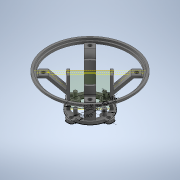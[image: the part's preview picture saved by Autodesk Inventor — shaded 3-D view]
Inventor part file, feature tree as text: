
AUTODESK INVENTOR PART (.ipt)
format: ipt  version: 2020 (Build 240168000, 168)  size: 606,208 bytes
history: native  units: mm
features: projected_geometry x28, sketch x16, extrude x9, other x5, pattern_circular x1, sweep x1
ambient origin geometry x8: Origin, YZ Plane, XZ Plane, XY Plane, X Axis, Y Axis, Z Axis, Center Point
bodies: Body1 (feature_tree)
feature tree (60):
  other  "Твердое тело1"
  sketch  "Эскиз1"
  extrude  "Выдавливание1"  Depth=44.0mm
  extrude  "Выдавливание2"  Depth=4.0mm
  sketch  "Эскиз3"
  extrude  "Выдавливание4"  Depth=40.0mm TaperAngle=360.0deg
  pattern_circular  "Круговой массив1"  [2 undecoded]
  other  "РабПлоскость2"
  sketch  "Эскиз5"
  other  "РабПлоскость1"
  sketch  "Эскиз6"
  sketch  "Эскиз7"
  extrude  "Выдавливание6"  Depth=4.5mm
  sketch  "Эскиз8"
  extrude  "Выдавливание7"  Depth=3.0mm
  sketch  "Эскиз9"
  other  "РабПлоскость3"
  sketch  "Эскиз10"
  sweep  "Сдвиг1"
  extrude  "Выдавливание8"  Depth=1.0mm
  extrude  "Выдавливание9"  TaperAngle=45.0deg  [1 undecoded]
  sketch  "Эскиз14"
  other  "РабПлоскость4"
  sketch  "Эскиз15"
  extrude  "Выдавливание10"  TaperAngle=135.0deg  [1 undecoded]
  extrude  "Выдавливание11"  Depth=34.0mm
  sketch  "Эскиз2"
  sketch  "Эскиз4"
  projected_geometry  "Спроецированная петля1"
  projected_geometry  "Спроецированная петля2"
  projected_geometry  "Спроецированная петля3"
  projected_geometry  "Спроецированная петля4"
  projected_geometry  "Спроецированная петля5"
  projected_geometry  "Спроецированная петля6"
  projected_geometry  "Спроецированная петля7"
  projected_geometry  "Спроецированная петля8"
  projected_geometry  "Спроецированная петля9"
  projected_geometry  "Спроецированная петля10"
  projected_geometry  "Спроецированная петля11"
  projected_geometry  "Спроецированная петля12"
  projected_geometry  "Спроецированная петля13"
  projected_geometry  "Спроецированная петля14"
  projected_geometry  "Спроецированная петля15"
  projected_geometry  "Спроецированная петля16"
  projected_geometry  "Спроецированная петля17"
  projected_geometry  "Спроецированная петля18"
  projected_geometry  "Спроецированная петля19"
  projected_geometry  "Спроецированная петля20"
  sketch  "Эскиз11"
  projected_geometry  "Спроецированная петля21"
  projected_geometry  "Спроецированная петля22"
  projected_geometry  "Спроецированная петля23"
  sketch  "3D эскиз1"
  sketch  "Эскиз12"
  sketch  "Эскиз13"
  projected_geometry  "Спроецированная петля24"
  projected_geometry  "Спроецированная петля25"
  projected_geometry  "Спроецированная петля26"
  projected_geometry  "Спроецированная петля27"
  projected_geometry  "Спроецированная петля28"
note: 4 required parameter values undecoded (feature->parameter linkage not recoverable at this tier; creation-order binding heuristic only, values carry confidence <= 0.55)
